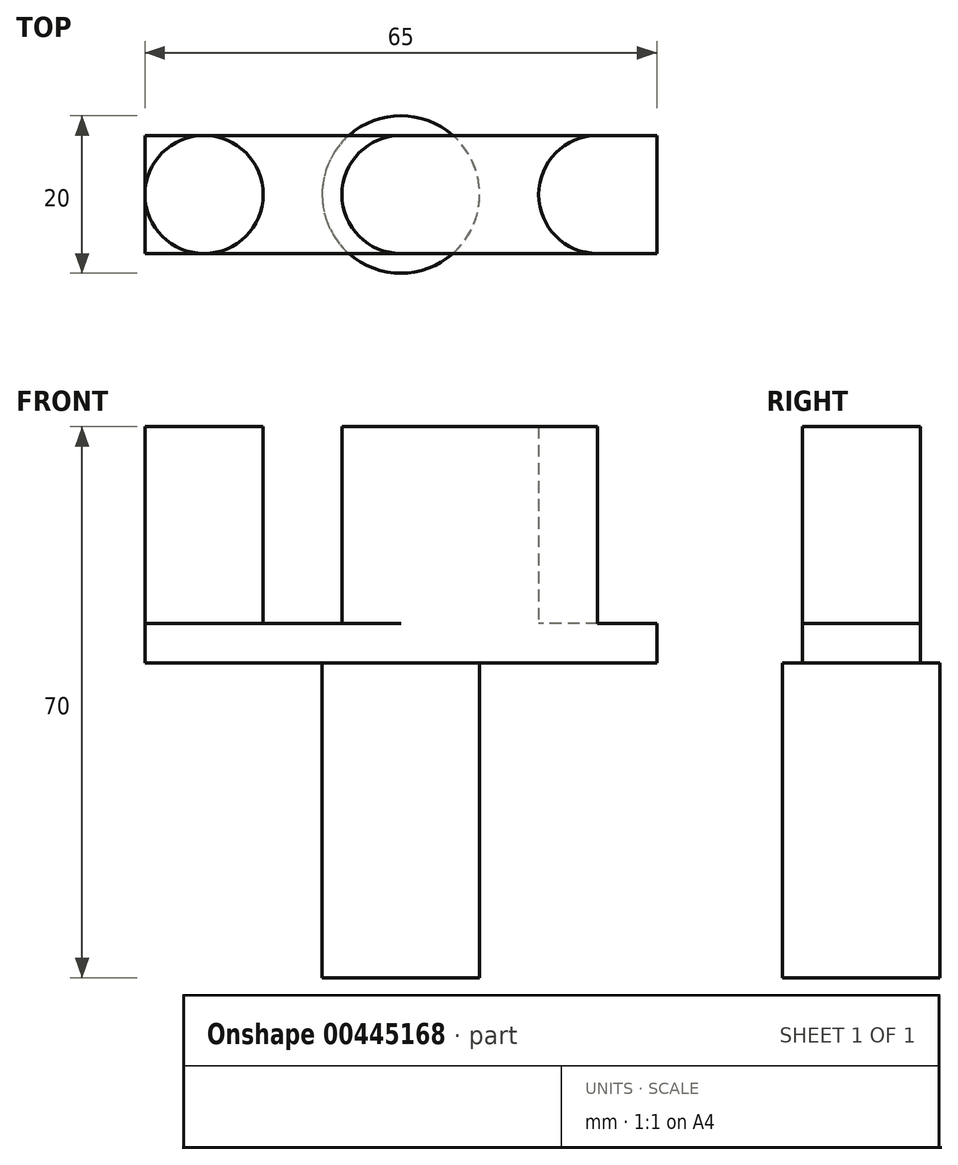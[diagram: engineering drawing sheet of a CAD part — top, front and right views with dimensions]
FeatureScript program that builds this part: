
annotation { "Feature Type Name" : "Feature", "Feature Type Description" : "" }
export const myFeature = defineFeature(function(context is Context, id is Id, definition is map)
    precondition{}
    {
        {
            var Q0;
            Q0=qCreatedBy(makeId("Top.planeOp"),FACE);
            var sketch = newSketch(context, id + "F0", { "sketchPlane" : qUnion([Q0])});
            skLineSegment(sketch, "E0.bottom", {"start": v(32.5, 7.5) * mm, "end": v(-32.5, 7.5) * mm});
            skLineSegment(sketch, "E0.top", {"start": v(32.5, -7.5) * mm, "end": v(-32.5, -7.5) * mm});
            skLineSegment(sketch, "E0.left", {"start": v(32.5, 7.5) * mm, "end": v(32.5, -7.5) * mm});
            skLineSegment(sketch, "E0.right", {"start": v(-32.5, 7.5) * mm, "end": v(-32.5, -7.5) * mm});
            skPoint(sketch, "E0.middle", {"position": v(0, 0) * mm});
            skCircle(sketch, "E1", {"center": v(0, 0) * mm, "radius": 7.5 * mm});
            skLineSegment(sketch, "E2", {"start": v(-17.5, 0) * mm, "end": v(-7.5, 0) * mm});
            skCircle(sketch, "E3", {"center": v(-25, 0) * mm, "radius": 7.5 * mm});
            skCircle(sketch, "E4.MirrorC", {"center": v(25, 0) * mm, "radius": 7.5 * mm});
            skSolve(sketch);
        }
        {
            var Q0;
            Q0 = qSketchRegion(id + "F0", true);
            extrude(context, id + "F1", {"entities" : qUnion([Q0]), "depth" : 5 * mm});
        }
        {
            var Q0;
            {var subQ0=sQuery(id+"F0.wireOp",EDGE,"E3");var subQ1=makeQuery(id+"F0.imprint","INTERSECT",VERTEX,{"derivedFrom":[sQuery(id+"F0.wireOp",EDGE,"E2"),subQ0]});Q0=makeQuery(id+"F0.imprint","IMPRINT",FACE,{"disambiguationData":[TD([[makeQuery(id+"F0.imprint","IMPRINT",EDGE,{"disambiguationData":[TD([[subQ1,-1.0]])],"derivedFrom":subQ0}),1.0]])]});}
            extrude(context, id + "F2", {"entities" : qUnion([Q0]), "operationType" : NewBodyOperationType.ADD, "depth" : 30 * mm});
        }
        {
            var Q0;
            {var subQ0=sQuery(id+"F0.wireOp",EDGE,"E1");var subQ1=makeQuery(id+"F0.imprint","INTERSECT",VERTEX,{"derivedFrom":[subQ0,sQuery(id+"F0.wireOp",EDGE,"E2")]});Q0=makeQuery(id+"F0.imprint","IMPRINT",FACE,{"disambiguationData":[TD([[makeQuery(id+"F0.imprint","IMPRINT",EDGE,{"disambiguationData":[TD([[subQ1,1.0]])],"derivedFrom":subQ0}),1.0]])]});}
            extrude(context, id + "F3", {"entities" : qUnion([Q0]), "operationType" : NewBodyOperationType.ADD, "depth" : 30 * mm});
        }
        {
            var Q0;
            {var subQ0=sQuery(id+"F0.wireOp",EDGE,"E4.MirrorC");var subQ1=makeQuery(id+"F0.imprint","INTERSECT",VERTEX,{"derivedFrom":[sQuery(id+"F0.wireOp",EDGE,"E0.bottom"),subQ0]});Q0=makeQuery(id+"F0.imprint","IMPRINT",FACE,{"disambiguationData":[TD([[makeQuery(id+"F0.imprint","IMPRINT",EDGE,{"disambiguationData":[TD([[subQ1,-1.0]])],"derivedFrom":subQ0}),-1.0]])]});}
            extrude(context, id + "F4", {"entities" : qUnion([Q0]), "operationType" : NewBodyOperationType.ADD, "depth" : 30 * mm});
        }
        {
            var Q0;
            Q0=makeQuery(id+"F1.opExtrude","CAP_FACE",FACE,{"disambiguationData":[OSD([sQuery(id+"F0.wireOp",EDGE,"E0.bottom"),sQuery(id+"F0.wireOp",EDGE,"E0.top"),sQuery(id+"F0.wireOp",EDGE,"E0.left"),sQuery(id+"F0.wireOp",EDGE,"E0.right")])],"isStart":true});
            var sketch = newSketch(context, id + "F5", { "sketchPlane" : qUnion([Q0])});
            skCircle(sketch, "E5", {"center": v(0, 0) * mm, "radius": 10 * mm});
            skSolve(sketch);
        }
        {
            var Q0;
            Q0 = qSketchRegion(id + "F5", true);
            extrude(context, id + "F6", {"entities" : qUnion([Q0]), "operationType" : NewBodyOperationType.ADD, "depth" : 40 * mm});
        }
    });
